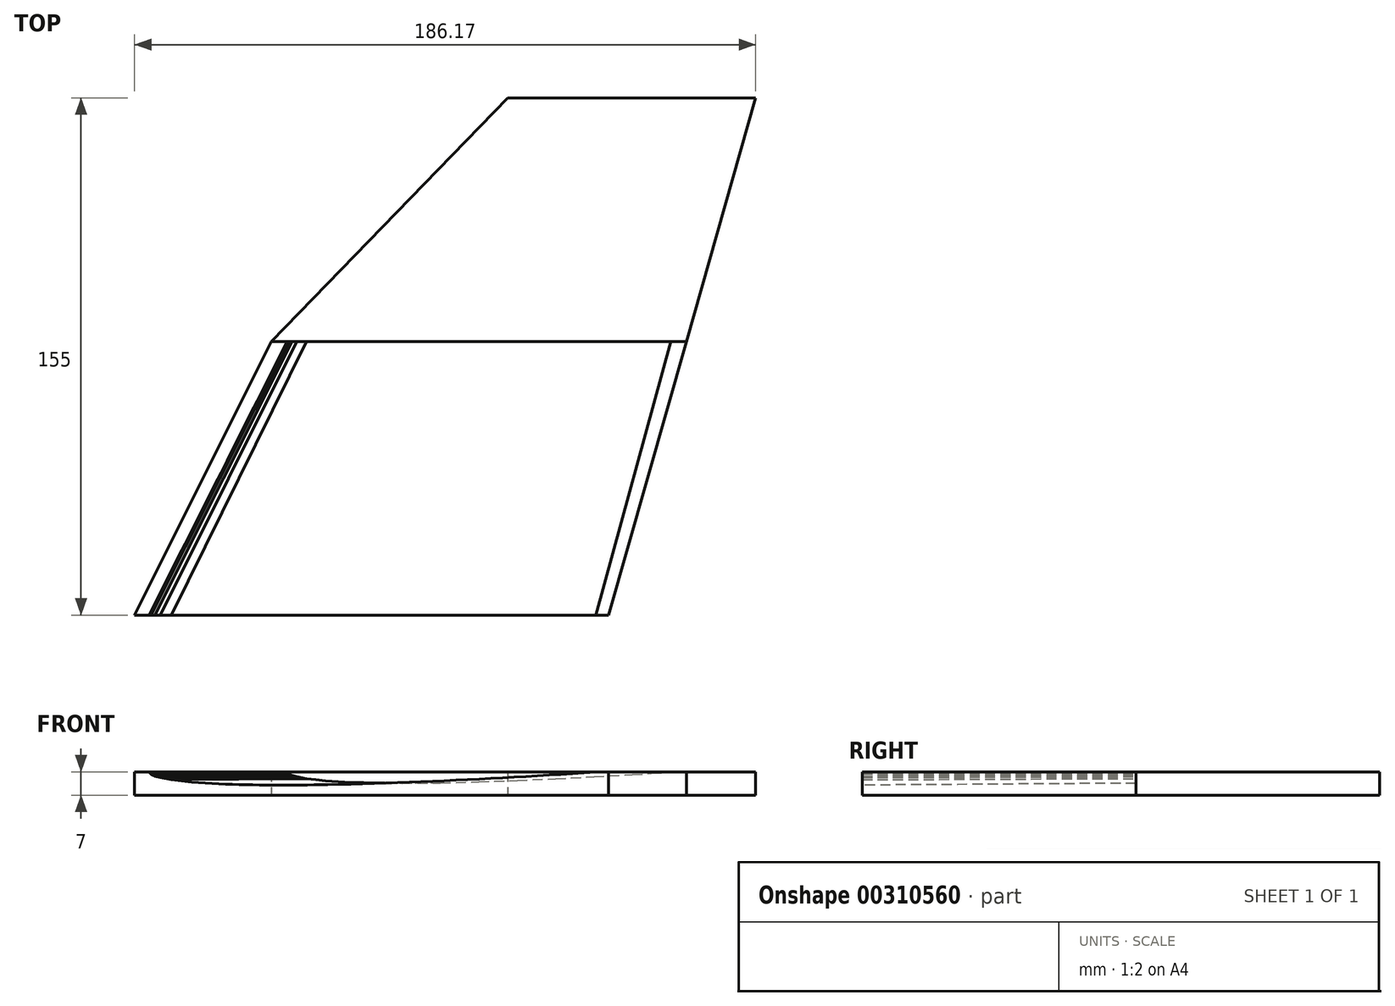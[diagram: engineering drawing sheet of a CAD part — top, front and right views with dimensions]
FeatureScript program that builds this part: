
annotation { "Feature Type Name" : "Feature", "Feature Type Description" : "" }
export const myFeature = defineFeature(function(context is Context, id is Id, definition is map)
    precondition{}
    {
        {
            var Q0;
            Q0=qCreatedBy(makeId("Front.planeOp"),FACE);
            cPlane(context, id + "F0", {"entities" : qUnion([Q0]), "cplaneType" : CPlaneType.OFFSET, "offset" : 242 * mm, "oppositeDirection" : true, "width" : 150 * mm, "height" : 150 * mm});
        }
        {
            var Q0;
            Q0=qCreatedBy(makeId("Front.planeOp"),FACE);
            cPlane(context, id + "F1", {"entities" : qUnion([Q0]), "cplaneType" : CPlaneType.OFFSET, "offset" : 315 * mm, "oppositeDirection" : true, "width" : 150 * mm, "height" : 150 * mm});
        }
        {
            var Q0;
            Q0=qCreatedBy(makeId("Front.planeOp"),FACE);
            var sketch = newSketch(context, id + "F2", { "sketchPlane" : qUnion([Q0])});
            skLineSegment(sketch, "E0", {"start": v(85.33, 0.1) * mm, "end": v(76.8, 0.69) * mm});
            skLineSegment(sketch, "E1", {"start": v(76.8, 0.69) * mm, "end": v(68.27, 1.23) * mm});
            skLineSegment(sketch, "E2", {"start": v(68.27, 1.23) * mm, "end": v(51.2, 2.24) * mm});
            skLineSegment(sketch, "E3", {"start": v(51.2, 2.24) * mm, "end": v(34.13, 3.12) * mm});
            skLineSegment(sketch, "E4", {"start": v(34.13, 3.12) * mm, "end": v(17.07, 3.9) * mm});
            skLineSegment(sketch, "E5", {"start": v(17.07, 3.9) * mm, "end": v(0, 4.51) * mm});
            skLineSegment(sketch, "E6", {"start": v(0, 4.51) * mm, "end": v(-17.07, 4.95) * mm});
            skLineSegment(sketch, "E7", {"start": v(-17.07, 4.95) * mm, "end": v(-34.13, 5.12) * mm});
            skLineSegment(sketch, "E8", {"start": v(-34.13, 5.12) * mm, "end": v(-42.67, 5.07) * mm});
            skLineSegment(sketch, "E9", {"start": v(-42.67, 5.07) * mm, "end": v(-51.2, 4.9) * mm});
            skLineSegment(sketch, "E10", {"start": v(-51.2, 4.9) * mm, "end": v(-59.73, 4.56) * mm});
            skLineSegment(sketch, "E11", {"start": v(-59.73, 4.56) * mm, "end": v(-68.27, 4) * mm});
            skLineSegment(sketch, "E12", {"start": v(-68.27, 4) * mm, "end": v(-72.53, 3.58) * mm});
            skLineSegment(sketch, "E13", {"start": v(-72.53, 3.58) * mm, "end": v(-76.8, 3.03) * mm});
            skLineSegment(sketch, "E14", {"start": v(-76.8, 3.03) * mm, "end": v(-81.07, 2.23) * mm});
            skLineSegment(sketch, "E15", {"start": v(-81.07, 2.23) * mm, "end": v(-83.2, 1.62) * mm});
            skLineSegment(sketch, "E16", {"start": v(-83.2, 1.62) * mm, "end": v(-84.61, 0.9) * mm});
            skLineSegment(sketch, "E17", {"start": v(-84.61, 0.9) * mm, "end": v(-85.33, 0) * mm});
            skLineSegment(sketch, "E18", {"start": v(-85.33, 0) * mm, "end": v(-84.68, -0.91) * mm});
            skLineSegment(sketch, "E19", {"start": v(-84.68, -0.91) * mm, "end": v(-83.2, -1.62) * mm});
            skLineSegment(sketch, "E20", {"start": v(-83.2, -1.62) * mm, "end": v(-81.07, -2.23) * mm});
            skLineSegment(sketch, "E21", {"start": v(-81.07, -2.23) * mm, "end": v(-76.8, -3.03) * mm});
            skLineSegment(sketch, "E22", {"start": v(-76.8, -3.03) * mm, "end": v(-72.53, -3.58) * mm});
            skLineSegment(sketch, "E23", {"start": v(-72.53, -3.58) * mm, "end": v(-68.27, -4) * mm});
            skLineSegment(sketch, "E24", {"start": v(-68.27, -4) * mm, "end": v(-59.73, -4.56) * mm});
            skLineSegment(sketch, "E25", {"start": v(-59.73, -4.56) * mm, "end": v(-51.2, -4.9) * mm});
            skLineSegment(sketch, "E26", {"start": v(-51.2, -4.9) * mm, "end": v(-42.67, -5.07) * mm});
            skLineSegment(sketch, "E27", {"start": v(-42.67, -5.07) * mm, "end": v(-34.13, -5.12) * mm});
            skLineSegment(sketch, "E28", {"start": v(-34.13, -5.12) * mm, "end": v(-17.07, -4.95) * mm});
            skLineSegment(sketch, "E29", {"start": v(-17.07, -4.95) * mm, "end": v(0, -4.51) * mm});
            skLineSegment(sketch, "E30", {"start": v(0, -4.51) * mm, "end": v(17.07, -3.9) * mm});
            skLineSegment(sketch, "E31", {"start": v(17.07, -3.9) * mm, "end": v(34.13, -3.12) * mm});
            skLineSegment(sketch, "E32", {"start": v(34.13, -3.12) * mm, "end": v(51.2, -2.24) * mm});
            skLineSegment(sketch, "E33", {"start": v(51.2, -2.24) * mm, "end": v(68.27, -1.23) * mm});
            skLineSegment(sketch, "E34", {"start": v(68.27, -1.23) * mm, "end": v(76.8, -0.69) * mm});
            skLineSegment(sketch, "E35", {"start": v(76.8, -0.69) * mm, "end": v(85.33, -0.1) * mm});
            skLineSegment(sketch, "E36", {"start": v(85.33, -0.1) * mm, "end": v(85.33, 0.1) * mm});
            skSolve(sketch);
        }
        {
            var Q0;
            Q0=qCreatedBy(id+"F0.planeOp",FACE);
            var sketch = newSketch(context, id + "F3", { "sketchPlane" : qUnion([Q0])});
            skLineSegment(sketch, "E37", {"start": v(151.77, 0.06) * mm, "end": v(146.02, 0.44) * mm});
            skLineSegment(sketch, "E38", {"start": v(146.02, 0.44) * mm, "end": v(140.27, 0.8) * mm});
            skLineSegment(sketch, "E39", {"start": v(140.27, 0.8) * mm, "end": v(128.77, 1.48) * mm});
            skLineSegment(sketch, "E40", {"start": v(128.77, 1.48) * mm, "end": v(117.27, 2.07) * mm});
            skLineSegment(sketch, "E41", {"start": v(117.27, 2.07) * mm, "end": v(105.77, 2.58) * mm});
            skLineSegment(sketch, "E42", {"start": v(105.77, 2.58) * mm, "end": v(94.27, 3) * mm});
            skLineSegment(sketch, "E43", {"start": v(94.27, 3) * mm, "end": v(82.77, 3.28) * mm});
            skLineSegment(sketch, "E44", {"start": v(82.77, 3.28) * mm, "end": v(71.27, 3.4) * mm});
            skLineSegment(sketch, "E45", {"start": v(71.27, 3.4) * mm, "end": v(65.52, 3.36) * mm});
            skLineSegment(sketch, "E46", {"start": v(65.52, 3.36) * mm, "end": v(59.77, 3.24) * mm});
            skLineSegment(sketch, "E47", {"start": v(59.77, 3.24) * mm, "end": v(54.02, 3.02) * mm});
            skLineSegment(sketch, "E48", {"start": v(54.02, 3.02) * mm, "end": v(48.27, 2.64) * mm});
            skLineSegment(sketch, "E49", {"start": v(48.27, 2.64) * mm, "end": v(45.4, 2.37) * mm});
            skLineSegment(sketch, "E50", {"start": v(45.4, 2.37) * mm, "end": v(42.52, 2) * mm});
            skLineSegment(sketch, "E51", {"start": v(42.52, 2) * mm, "end": v(39.65, 1.47) * mm});
            skLineSegment(sketch, "E52", {"start": v(39.65, 1.47) * mm, "end": v(38.2, 1.06) * mm});
            skLineSegment(sketch, "E53", {"start": v(38.2, 1.06) * mm, "end": v(37.26, 0.58) * mm});
            skLineSegment(sketch, "E54", {"start": v(37.26, 0.58) * mm, "end": v(36.77, -0.01) * mm});
            skLineSegment(sketch, "E55", {"start": v(36.77, -0.01) * mm, "end": v(37.21, -0.62) * mm});
            skLineSegment(sketch, "E56", {"start": v(37.21, -0.62) * mm, "end": v(38.2, -1.09) * mm});
            skLineSegment(sketch, "E57", {"start": v(38.2, -1.09) * mm, "end": v(39.65, -1.5) * mm});
            skLineSegment(sketch, "E58", {"start": v(39.65, -1.5) * mm, "end": v(42.52, -2.03) * mm});
            skLineSegment(sketch, "E59", {"start": v(42.52, -2.03) * mm, "end": v(45.4, -2.4) * mm});
            skLineSegment(sketch, "E60", {"start": v(45.4, -2.4) * mm, "end": v(48.27, -2.67) * mm});
            skLineSegment(sketch, "E61", {"start": v(48.27, -2.67) * mm, "end": v(54.02, -3.05) * mm});
            skLineSegment(sketch, "E62", {"start": v(54.02, -3.05) * mm, "end": v(59.77, -3.27) * mm});
            skLineSegment(sketch, "E63", {"start": v(59.77, -3.27) * mm, "end": v(65.52, -3.38) * mm});
            skLineSegment(sketch, "E64", {"start": v(65.52, -3.38) * mm, "end": v(71.27, -3.42) * mm});
            skLineSegment(sketch, "E65", {"start": v(71.27, -3.42) * mm, "end": v(82.77, -3.3) * mm});
            skLineSegment(sketch, "E66", {"start": v(82.77, -3.3) * mm, "end": v(94.27, -3.02) * mm});
            skLineSegment(sketch, "E67", {"start": v(94.27, -3.02) * mm, "end": v(105.77, -2.6) * mm});
            skLineSegment(sketch, "E68", {"start": v(105.77, -2.6) * mm, "end": v(117.27, -2.1) * mm});
            skLineSegment(sketch, "E69", {"start": v(117.27, -2.1) * mm, "end": v(128.77, -1.5) * mm});
            skLineSegment(sketch, "E70", {"start": v(128.77, -1.5) * mm, "end": v(140.27, -0.83) * mm});
            skLineSegment(sketch, "E71", {"start": v(140.27, -0.83) * mm, "end": v(146.02, -0.47) * mm});
            skLineSegment(sketch, "E72", {"start": v(146.02, -0.47) * mm, "end": v(151.77, -0.08) * mm});
            skLineSegment(sketch, "E73", {"start": v(151.77, -0.08) * mm, "end": v(151.77, 0.06) * mm});
            skSolve(sketch);
        }
        {
            var Q0;
            Q0=qCreatedBy(id+"F1.planeOp",FACE);
            var sketch = newSketch(context, id + "F4", { "sketchPlane" : qUnion([Q0])});
            skLineSegment(sketch, "E74", {"start": v(172.88, 0.04) * mm, "end": v(169.63, 0.25) * mm});
            skLineSegment(sketch, "E75", {"start": v(169.63, 0.25) * mm, "end": v(166.37, 0.45) * mm});
            skLineSegment(sketch, "E76", {"start": v(166.37, 0.45) * mm, "end": v(159.87, 0.82) * mm});
            skLineSegment(sketch, "E77", {"start": v(159.87, 0.82) * mm, "end": v(153.36, 1.14) * mm});
            skLineSegment(sketch, "E78", {"start": v(153.36, 1.14) * mm, "end": v(146.85, 1.42) * mm});
            skLineSegment(sketch, "E79", {"start": v(146.85, 1.42) * mm, "end": v(140.34, 1.65) * mm});
            skLineSegment(sketch, "E80", {"start": v(140.34, 1.65) * mm, "end": v(133.83, 1.8) * mm});
            skLineSegment(sketch, "E81", {"start": v(133.83, 1.8) * mm, "end": v(127.33, 1.87) * mm});
            skLineSegment(sketch, "E82", {"start": v(127.33, 1.87) * mm, "end": v(124.07, 1.85) * mm});
            skLineSegment(sketch, "E83", {"start": v(124.07, 1.85) * mm, "end": v(120.82, 1.79) * mm});
            skLineSegment(sketch, "E84", {"start": v(120.82, 1.79) * mm, "end": v(117.56, 1.67) * mm});
            skLineSegment(sketch, "E85", {"start": v(117.56, 1.67) * mm, "end": v(114.31, 1.46) * mm});
            skLineSegment(sketch, "E86", {"start": v(114.31, 1.46) * mm, "end": v(112.68, 1.3) * mm});
            skLineSegment(sketch, "E87", {"start": v(112.68, 1.3) * mm, "end": v(111.06, 1.1) * mm});
            skLineSegment(sketch, "E88", {"start": v(111.06, 1.1) * mm, "end": v(109.43, 0.81) * mm});
            skLineSegment(sketch, "E89", {"start": v(109.43, 0.81) * mm, "end": v(108.62, 0.6) * mm});
            skLineSegment(sketch, "E90", {"start": v(108.62, 0.6) * mm, "end": v(108.08, 0.33) * mm});
            skLineSegment(sketch, "E91", {"start": v(108.2, 0.47) * mm, "end": v(107.8, 0) * mm});
            skLineSegment(sketch, "E92", {"start": v(107.8, 0) * mm, "end": v(108.05, -0.33) * mm});
            skLineSegment(sketch, "E93", {"start": v(108.05, -0.33) * mm, "end": v(108.62, -0.6) * mm});
            skLineSegment(sketch, "E94", {"start": v(108.62, -0.6) * mm, "end": v(109.43, -0.81) * mm});
            skLineSegment(sketch, "E95", {"start": v(109.43, -0.81) * mm, "end": v(111.06, -1.1) * mm});
            skLineSegment(sketch, "E96", {"start": v(111.06, -1.1) * mm, "end": v(112.68, -1.3) * mm});
            skLineSegment(sketch, "E97", {"start": v(112.68, -1.3) * mm, "end": v(114.31, -1.46) * mm});
            skLineSegment(sketch, "E98", {"start": v(114.31, -1.46) * mm, "end": v(117.56, -1.67) * mm});
            skLineSegment(sketch, "E99", {"start": v(117.56, -1.67) * mm, "end": v(120.82, -1.79) * mm});
            skLineSegment(sketch, "E100", {"start": v(120.82, -1.79) * mm, "end": v(124.07, -1.85) * mm});
            skLineSegment(sketch, "E101", {"start": v(124.07, -1.85) * mm, "end": v(127.33, -1.87) * mm});
            skLineSegment(sketch, "E102", {"start": v(127.33, -1.87) * mm, "end": v(133.83, -1.8) * mm});
            skLineSegment(sketch, "E103", {"start": v(133.83, -1.8) * mm, "end": v(140.34, -1.65) * mm});
            skLineSegment(sketch, "E104", {"start": v(140.34, -1.65) * mm, "end": v(146.85, -1.42) * mm});
            skLineSegment(sketch, "E105", {"start": v(146.85, -1.42) * mm, "end": v(153.36, -1.14) * mm});
            skLineSegment(sketch, "E106", {"start": v(153.36, -1.14) * mm, "end": v(159.87, -0.82) * mm});
            skLineSegment(sketch, "E107", {"start": v(159.87, -0.82) * mm, "end": v(166.37, -0.45) * mm});
            skLineSegment(sketch, "E108", {"start": v(166.37, -0.45) * mm, "end": v(169.63, -0.25) * mm});
            skLineSegment(sketch, "E109", {"start": v(169.63, -0.25) * mm, "end": v(172.88, -0.04) * mm});
            skLineSegment(sketch, "E110", {"start": v(172.88, -0.04) * mm, "end": v(172.88, 0.04) * mm});
            skSolve(sketch);
        }
        {
            var Q0;
            Q0=makeQuery(id+"F2.imprint","IMPRINT",FACE,{"disambiguationData":[TD([[makeQuery(id+"F2.imprint","IMPRINT",EDGE,{"derivedFrom":sQuery(id+"F2.wireOp",EDGE,"E0")}),1.0]])]});
            var Q1;
            Q1=makeQuery(id+"F3.imprint","IMPRINT",FACE,{"disambiguationData":[TD([[makeQuery(id+"F3.imprint","IMPRINT",EDGE,{"derivedFrom":sQuery(id+"F3.wireOp",EDGE,"E37")}),1.0]])]});
            loft(context, id + "F5", {"sheetProfilesArray" : [{ "sheetProfileEntities" : qUnion([Q0]) }, { "sheetProfileEntities" : qUnion([Q1]) }]});
        }
        {
            var Q0;
            Q0=qCreatedBy(makeId("Front.planeOp"),FACE);
            var sketch = newSketch(context, id + "F6", { "sketchPlane" : qUnion([Q0])});
            skLineSegment(sketch, "E111.bottom", {"start": v(-88.87, 0) * mm, "end": v(61.07, 0) * mm});
            skLineSegment(sketch, "E112.bottom", {"start": v(-88.87, 0) * mm, "end": v(87.49, 0) * mm});
            skLineSegment(sketch, "E112.top", {"start": v(-88.87, -7) * mm, "end": v(87.49, -7) * mm});
            skLineSegment(sketch, "E112.left", {"start": v(-88.87, 0) * mm, "end": v(-88.87, -7) * mm});
            skLineSegment(sketch, "E112.right", {"start": v(87.49, 0) * mm, "end": v(87.49, -7) * mm});
            skSolve(sketch);
        }
        {
            var Q0;
            Q0=qCreatedBy(id+"F0.planeOp",FACE);
            var sketch = newSketch(context, id + "F7", { "sketchPlane" : qUnion([Q0])});
            skLineSegment(sketch, "E113.bottom", {"start": v(32, 0) * mm, "end": v(156.45, 0) * mm});
            skLineSegment(sketch, "E113.top", {"start": v(32, -7) * mm, "end": v(156.45, -7) * mm});
            skLineSegment(sketch, "E113.left", {"start": v(32, 0) * mm, "end": v(32, -7) * mm});
            skLineSegment(sketch, "E113.right", {"start": v(156.45, 0) * mm, "end": v(156.45, -7) * mm});
            skSolve(sketch);
        }
        {
            var Q1;
            Q1=qSketchRegion(id+"F3",true);
            var Q2;
            Q2=makeQuery(id+"F4.imprint","IMPRINT",FACE,{"disambiguationData":[TD([[makeQuery(id+"F4.imprint","IMPRINT",EDGE,{"derivedFrom":sQuery(id+"F4.wireOp",EDGE,"E74")}),1.0]])]});
            loft(context, id + "F8", {"operationType" : NewBodyOperationType.ADD, "sheetProfilesArray" : [{ "sheetProfileEntities" : qUnion([Q1]) }, { "sheetProfileEntities" : qUnion([Q2]) }]});
        }
        {
            var Q0;
            Q0=qCreatedBy(id+"F1.planeOp",FACE);
            var sketch = newSketch(context, id + "F9", { "sketchPlane" : qUnion([Q0])});
            skLineSegment(sketch, "E114.bottom", {"start": v(177.22, 0) * mm, "end": v(102.9, 0) * mm});
            skLineSegment(sketch, "E114.top", {"start": v(177.22, -7) * mm, "end": v(102.9, -7) * mm});
            skLineSegment(sketch, "E114.left", {"start": v(177.22, 0) * mm, "end": v(177.22, -7) * mm});
            skLineSegment(sketch, "E114.right", {"start": v(102.9, 0) * mm, "end": v(102.9, -7) * mm});
            skSolve(sketch);
        }
        {
            var Q1;
            Q1=makeQuery(id+"F6.imprint","IMPRINT",FACE,{"disambiguationData":[TD([[makeQuery(id+"F6.imprint","IMPRINT",EDGE,{"derivedFrom":sQuery(id+"F6.wireOp",EDGE,"E112.bottom")}),-1.0]])]});
            var Q2;
            Q2=makeQuery(id+"F7.imprint","IMPRINT",FACE,{"disambiguationData":[TD([[makeQuery(id+"F7.imprint","IMPRINT",EDGE,{"derivedFrom":sQuery(id+"F7.wireOp",EDGE,"E113.bottom")}),-1.0]])]});
            loft(context, id + "F10", {"sheetProfilesArray" : [{ "sheetProfileEntities" : qUnion([Q1]) }, { "sheetProfileEntities" : qUnion([Q2]) }]});
        }
        {
            var Q1;
            Q1=makeQuery(id+"F9.imprint","IMPRINT",FACE,{"disambiguationData":[TD([[makeQuery(id+"F9.imprint","IMPRINT",EDGE,{"derivedFrom":sQuery(id+"F9.wireOp",EDGE,"E114.top")}),-1.0]])]});
            var Q2;
            Q2=makeQuery(id+"F7.imprint","IMPRINT",FACE,{"disambiguationData":[TD([[makeQuery(id+"F7.imprint","IMPRINT",EDGE,{"derivedFrom":sQuery(id+"F7.wireOp",EDGE,"E113.bottom")}),-1.0]])]});
            loft(context, id + "F11", {"sheetProfilesArray" : [{ "sheetProfileEntities" : qUnion([Q1]) }, { "sheetProfileEntities" : qUnion([Q2]) }]});
        }
        {
            var Q0;
            Q0=makeQuery(id+"F5.opLoft","SWEPT_BODY",BODY,{"disambiguationData":[OSD([makeQuery(id+"F2.imprint","IMPRINT",FACE,{"disambiguationData":[TD([[makeQuery(id+"F2.imprint","IMPRINT",EDGE,{"derivedFrom":sQuery(id+"F2.wireOp",EDGE,"E0")}),1.0]])]}),makeQuery(id+"F3.imprint","IMPRINT",FACE,{"disambiguationData":[TD([[makeQuery(id+"F3.imprint","IMPRINT",EDGE,{"derivedFrom":sQuery(id+"F3.wireOp",EDGE,"E37")}),1.0]])]})])]});
            var Q1;
            Q1=makeQuery(id+"F10.opLoft","SWEPT_BODY",BODY,{"disambiguationData":[OSD([makeQuery(id+"F6.imprint","IMPRINT",FACE,{"disambiguationData":[TD([[makeQuery(id+"F6.imprint","IMPRINT",EDGE,{"derivedFrom":sQuery(id+"F6.wireOp",EDGE,"E112.bottom")}),-1.0]])]}),makeQuery(id+"F7.imprint","IMPRINT",FACE,{"disambiguationData":[TD([[makeQuery(id+"F7.imprint","IMPRINT",EDGE,{"derivedFrom":sQuery(id+"F7.wireOp",EDGE,"E113.bottom")}),-1.0]])]})])]});
            booleanBodies(context, id + "F12", {"operationType" : BooleanOperationType.SUBTRACTION, "tools" : qUnion([Q0]), "targets" : qUnion([Q1])});
        }
        {
            var Q0;
            Q0=qCreatedBy(makeId("Front.planeOp"),FACE);
            cPlane(context, id + "F13", {"entities" : qUnion([Q0]), "cplaneType" : CPlaneType.OFFSET, "offset" : 160 * mm, "oppositeDirection" : true, "width" : 150 * mm, "height" : 150 * mm});
        }
        {
            var Q0;
            Q0=qCreatedBy(id+"F13.planeOp",FACE);
            var sketch = newSketch(context, id + "F14", { "sketchPlane" : qUnion([Q0])});
            skLineSegment(sketch, "E115.bottom", {"start": v(-91.18, 11.32) * mm, "end": v(184.82, 11.32) * mm});
            skLineSegment(sketch, "E115.top", {"start": v(-91.18, -19.62) * mm, "end": v(184.82, -19.62) * mm});
            skLineSegment(sketch, "E115.left", {"start": v(-91.18, 11.32) * mm, "end": v(-91.18, -19.62) * mm});
            skLineSegment(sketch, "E115.right", {"start": v(184.82, 11.32) * mm, "end": v(184.82, -19.62) * mm});
            skSolve(sketch);
        }
        {
            var Q0;
            Q0=makeQuery(id+"F14.imprint","IMPRINT",FACE,{"disambiguationData":[TD([[makeQuery(id+"F14.imprint","IMPRINT",EDGE,{"derivedFrom":sQuery(id+"F14.wireOp",EDGE,"E115.bottom")}),-1.0]])]});
            extrude(context, id + "F15", {"entities" : qUnion([Q0]), "operationType" : NewBodyOperationType.REMOVE, "depth" : 200 * mm});
        }
    });
